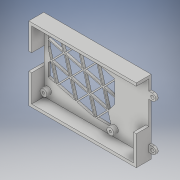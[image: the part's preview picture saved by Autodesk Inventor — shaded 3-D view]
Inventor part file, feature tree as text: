
AUTODESK INVENTOR PART (.ipt)
format: ipt  version: 2019 (Build 230136000, 136)  size: 582,144 bytes
history: native  units: in
note: dims shown in document units (in); Inventor stores cm internally (conversion verified against a paired STEP export)
features: extrude x5, sketch x2
ambient origin geometry x8: Origin, YZ Plane, XZ Plane, XY Plane, X Axis, Y Axis, Z Axis, Center Point
bodies: Solid1 (feature_tree)
feature tree (7):
  sketch  "Sketch1"  dims[d0=0.0787in d1=0.0787in]
  extrude  "Extrusion1"  Depth=0.0787in
  extrude  "Extrusion2"  Depth=0.0787in
  extrude  "Extrusion3"  Depth=0.0787in
  extrude  "Extrusion4"  Depth=1.9291in
  extrude  "Extrusion5"  Depth=0.2362in
  sketch  "Sketch2"  dims[d2=2.2835in d3=0.0787in d4=0.0787in d5=1.9291in d6=0.2362in d7=0.2362in d8=0.2362in d9=0.2362in d10=0.126in d11=0.0984in d12=0.126in d14=0.5906in d17=0.2559in d18=0.0984in d19=1.1614in d20=0.126in d21=0.0984in d22=0.6496in d23=0.1181in d24=0.1181in d25=0.2362in d26=0.1181in d27=0.1181in d28=0.2362in d29=0.3543in d30=0.1181in d31=0.2362in d32=0.1181in d33=0.1181in d34=0.2362in d35=0.0984in d36=0.1181in d37=0.0787in d38=0.0in d39=0.2362in d40=0.0in d41=0.0984in d42=0.0984in d43=0.5118in d44=0.0in d45=0.5118in d46=0.0in d62=0.5906in d63=0.5906in d64=0.5906in d66=0.5906in d67=0.5906in d68=0.5906in d69=0.0866in d73=0.0866in d75=0.5906in d76=0.0433in d77=0.5906in d78=0.0433in d79=0.5906in d81=0.5906in d82=0.5906in d83=0.5906in d84=0.0433in d85=0.0375in d86=60.0deg d87=0.0375in d88=0.5906in d90=60.0deg d91=60.0deg d92=60.0deg d93=0.0433in d94=60.0deg d95=60.0deg d96=0.0433in d97=60.0deg d98=0.5118in d99=0.0in]
